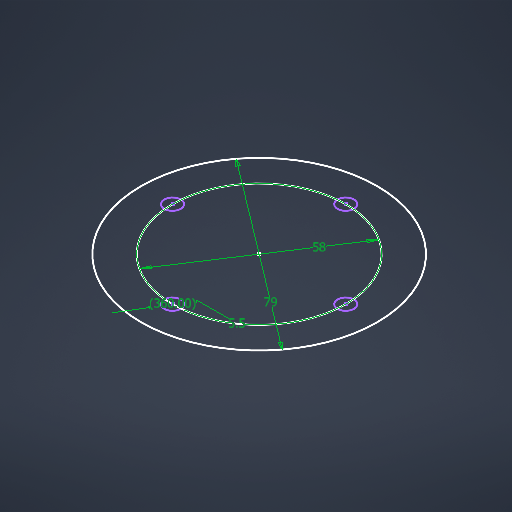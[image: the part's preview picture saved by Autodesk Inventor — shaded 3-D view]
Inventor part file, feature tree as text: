
AUTODESK INVENTOR PART (.ipt)
format: ipt  version: 2025 (Build 290162000, 162)  size: 200,192 bytes
history: native  units: in
note: dims shown in document units (in); Inventor stores cm internally (conversion verified against a paired STEP export)
features: sketch x2
ambient origin geometry x8: Origin, YZ Plane, XZ Plane, XY Plane, X Axis, Y Axis, Z Axis, Center Point
feature tree (2):
  sketch  "Sketch1"  dims[d0=2.2835in]
  sketch  "Sketch Circular Pattern1"  dims[d1=3.1102in d2=0.2165in d3=1.5748in d5=360.0deg d7=0.0197in d8=0.0344in d9=0.0197in d10=0.0344in]
